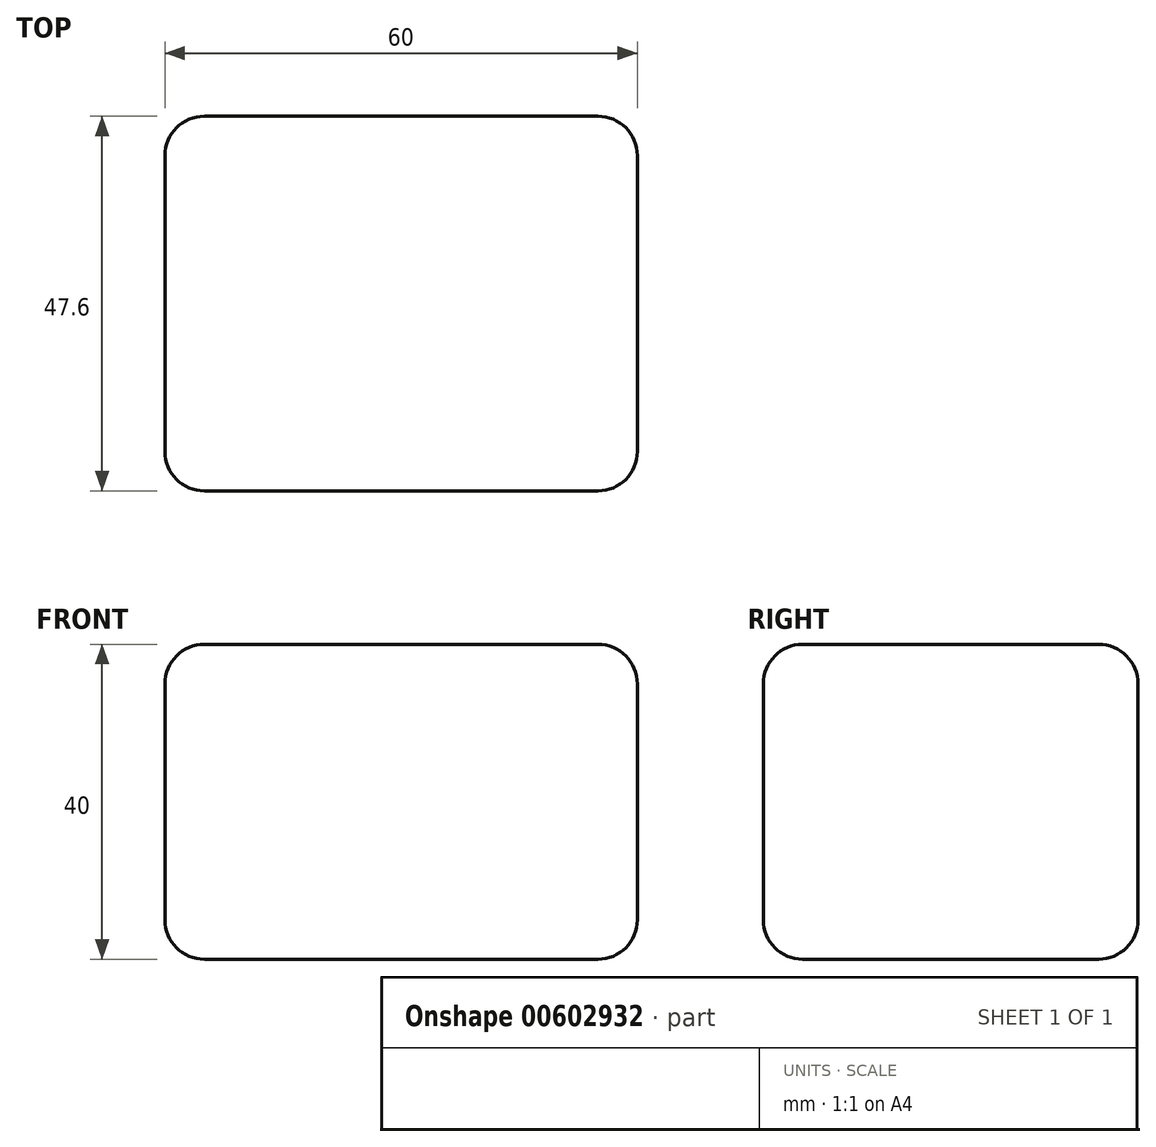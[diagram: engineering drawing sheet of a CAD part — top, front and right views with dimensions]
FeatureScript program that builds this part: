
annotation { "Feature Type Name" : "Feature", "Feature Type Description" : "" }
export const myFeature = defineFeature(function(context is Context, id is Id, definition is map)
    precondition{}
    {
        {
            var Q0;
            Q0=qCreatedBy(makeId("Front.planeOp"),FACE);
            var sketch = newSketch(context, id + "F0", { "sketchPlane" : qUnion([Q0])});
            skLineSegment(sketch, "E0.bottom", {"start": v(0, 0) * mm, "end": v(-60, 0) * mm});
            skLineSegment(sketch, "E0.top", {"start": v(0, 40) * mm, "end": v(-60, 40) * mm});
            skLineSegment(sketch, "E0.left", {"start": v(0, 0) * mm, "end": v(0, 40) * mm});
            skLineSegment(sketch, "E0.right", {"start": v(-60, 0) * mm, "end": v(-60, 40) * mm});
            skSolve(sketch);
        }
        {
            var Q0;
            Q0 = qSketchRegion(id + "F0", true);
            extrude(context, id + "F1", {"entities" : qUnion([Q0]), "depth" : 47.6 * mm, "offsetDistance" : 25 * mm});
        }
        {
            var Q0;
            Q0=makeQuery(id+"F1.opExtrude","SWEPT_EDGE",EDGE,{"disambiguationData":[OSD([sQuery(id+"F0.wireOp",EDGE,"E0.top"),sQuery(id+"F0.wireOp",EDGE,"E0.right")])]});
            var Q1;
            Q1=makeQuery(id+"F1.opExtrude","CAP_EDGE",EDGE,{"disambiguationData":[OSD([sQuery(id+"F0.wireOp",EDGE,"E0.right")])],"isStart":false});
            var Q2;
            Q2=makeQuery(id+"F1.opExtrude","SWEPT_FACE",FACE,{"disambiguationData":[OSD([sQuery(id+"F0.wireOp",EDGE,"E0.right")])]});
            fillet(context, id + "F2", {"entities" : qUnion([Q0, Q1, Q2]), "radius" : 5 * mm, "tangentPropagation" : true, "allowEdgeOverflow" : false});
        }
        {
            var Q0;
            Q0=makeQuery(id+"F1.opExtrude","CAP_EDGE",EDGE,{"disambiguationData":[OSD([sQuery(id+"F0.wireOp",EDGE,"E0.top")])],"isStart":false});
            var Q1;
            Q1=makeQuery(id+"F1.opExtrude","CAP_EDGE",EDGE,{"disambiguationData":[OSD([sQuery(id+"F0.wireOp",EDGE,"E0.top")])],"isStart":true});
            var Q2;
            Q2=makeQuery(id+"F1.opExtrude","SWEPT_EDGE",EDGE,{"disambiguationData":[OSD([sQuery(id+"F0.wireOp",EDGE,"E0.top"),sQuery(id+"F0.wireOp",EDGE,"E0.left")])]});
            var Q3;
            Q3=makeQuery(id+"F1.opExtrude","SWEPT_EDGE",EDGE,{"disambiguationData":[OSD([sQuery(id+"F0.wireOp",EDGE,"E0.bottom"),sQuery(id+"F0.wireOp",EDGE,"E0.left")])]});
            var Q4;
            Q4=makeQuery(id+"F1.opExtrude","CAP_EDGE",EDGE,{"disambiguationData":[OSD([sQuery(id+"F0.wireOp",EDGE,"E0.left")])],"isStart":true});
            var Q5;
            Q5=makeQuery(id+"F1.opExtrude","CAP_EDGE",EDGE,{"disambiguationData":[OSD([sQuery(id+"F0.wireOp",EDGE,"E0.left")])],"isStart":false});
            var Q6;
            Q6=makeQuery(id+"F1.opExtrude","CAP_EDGE",EDGE,{"disambiguationData":[OSD([sQuery(id+"F0.wireOp",EDGE,"E0.bottom")])],"isStart":false});
            var Q7;
            Q7=makeQuery(id+"F1.opExtrude","CAP_EDGE",EDGE,{"disambiguationData":[OSD([sQuery(id+"F0.wireOp",EDGE,"E0.bottom")])],"isStart":true});
            var Q8;
            {var subQ0=sQuery(id+"F0.wireOp",EDGE,"E0.right");Q8=makeQuery(id+"F2.opFillet","BLEND_EDGE",EDGE,{"blendedFrom":[makeQuery(id+"F1.opExtrude","CAP_EDGE",EDGE,{"disambiguationData":[OSD([subQ0])],"isStart":true}),makeQuery(id+"F1.opExtrude","CAP_FACE",FACE,{"disambiguationData":[OSD([sQuery(id+"F0.wireOp",EDGE,"E0.bottom"),sQuery(id+"F0.wireOp",EDGE,"E0.top"),sQuery(id+"F0.wireOp",EDGE,"E0.left"),subQ0])],"isStart":true})],"blendedInto":[makeQuery(id+"F1.opExtrude","CAP_FACE",FACE,{"disambiguationData":[OSD([sQuery(id+"F0.wireOp",EDGE,"E0.bottom"),sQuery(id+"F0.wireOp",EDGE,"E0.top"),sQuery(id+"F0.wireOp",EDGE,"E0.left"),subQ0])],"isStart":true})]});}
            var Q9;
            {var subQ0=sQuery(id+"F0.wireOp",EDGE,"E0.bottom");Q9=makeQuery(id+"F2.opFillet","BLEND_EDGE",EDGE,{"blendedFrom":[makeQuery(id+"F1.opExtrude","SWEPT_EDGE",EDGE,{"disambiguationData":[OSD([subQ0,sQuery(id+"F0.wireOp",EDGE,"E0.right")])]}),makeQuery(id+"F1.opExtrude","SWEPT_FACE",FACE,{"disambiguationData":[OSD([subQ0])]})],"blendedInto":[makeQuery(id+"F1.opExtrude","SWEPT_FACE",FACE,{"disambiguationData":[OSD([subQ0])]})]});}
            fillet(context, id + "F3", {"entities" : qUnion([Q0, Q1, Q2, Q3, Q4, Q5, Q6, Q7, Q8, Q9]), "radius" : 5 * mm, "tangentPropagation" : true, "allowEdgeOverflow" : false});
        }
    });
